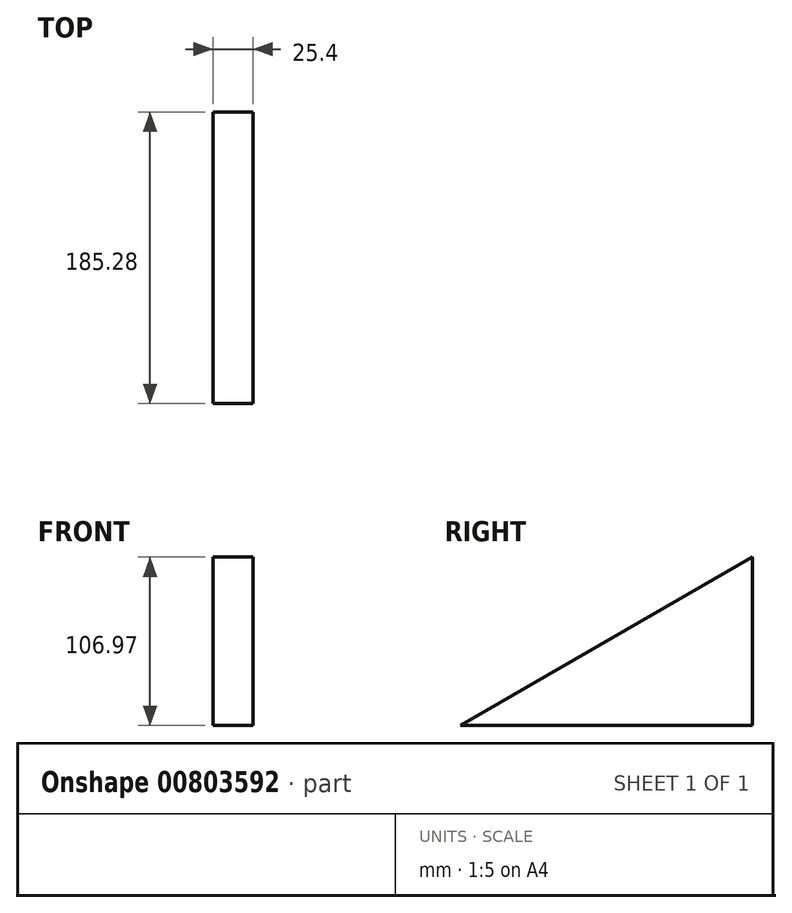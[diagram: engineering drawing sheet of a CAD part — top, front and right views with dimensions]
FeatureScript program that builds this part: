
annotation { "Feature Type Name" : "Feature", "Feature Type Description" : "" }
export const myFeature = defineFeature(function(context is Context, id is Id, definition is map)
    precondition{}
    {
        {
            var Q0;
            Q0=qCreatedBy(makeId("Right.planeOp"),FACE);
            var sketch = newSketch(context, id + "F0", { "sketchPlane" : qUnion([Q0])});
            skLineSegment(sketch, "E0", {"start": v(-185.28, 0) * mm, "end": v(0, 106.97) * mm});
            skLineSegment(sketch, "E1", {"start": v(-185.28, 0) * mm, "end": v(0, 0) * mm});
            skLineSegment(sketch, "E2", {"start": v(0, 0) * mm, "end": v(0, 106.97) * mm});
            skSolve(sketch);
        }
        {
            var Q0;
            Q0 = qSketchRegion(id + "F0", true);
            extrude(context, id + "F1", {"entities" : qUnion([Q0]), "endBound" : BoundingType.SYMMETRIC, "depth" : 25.4 * mm, "offsetDistance" : 25.4 * mm});
        }
    });
